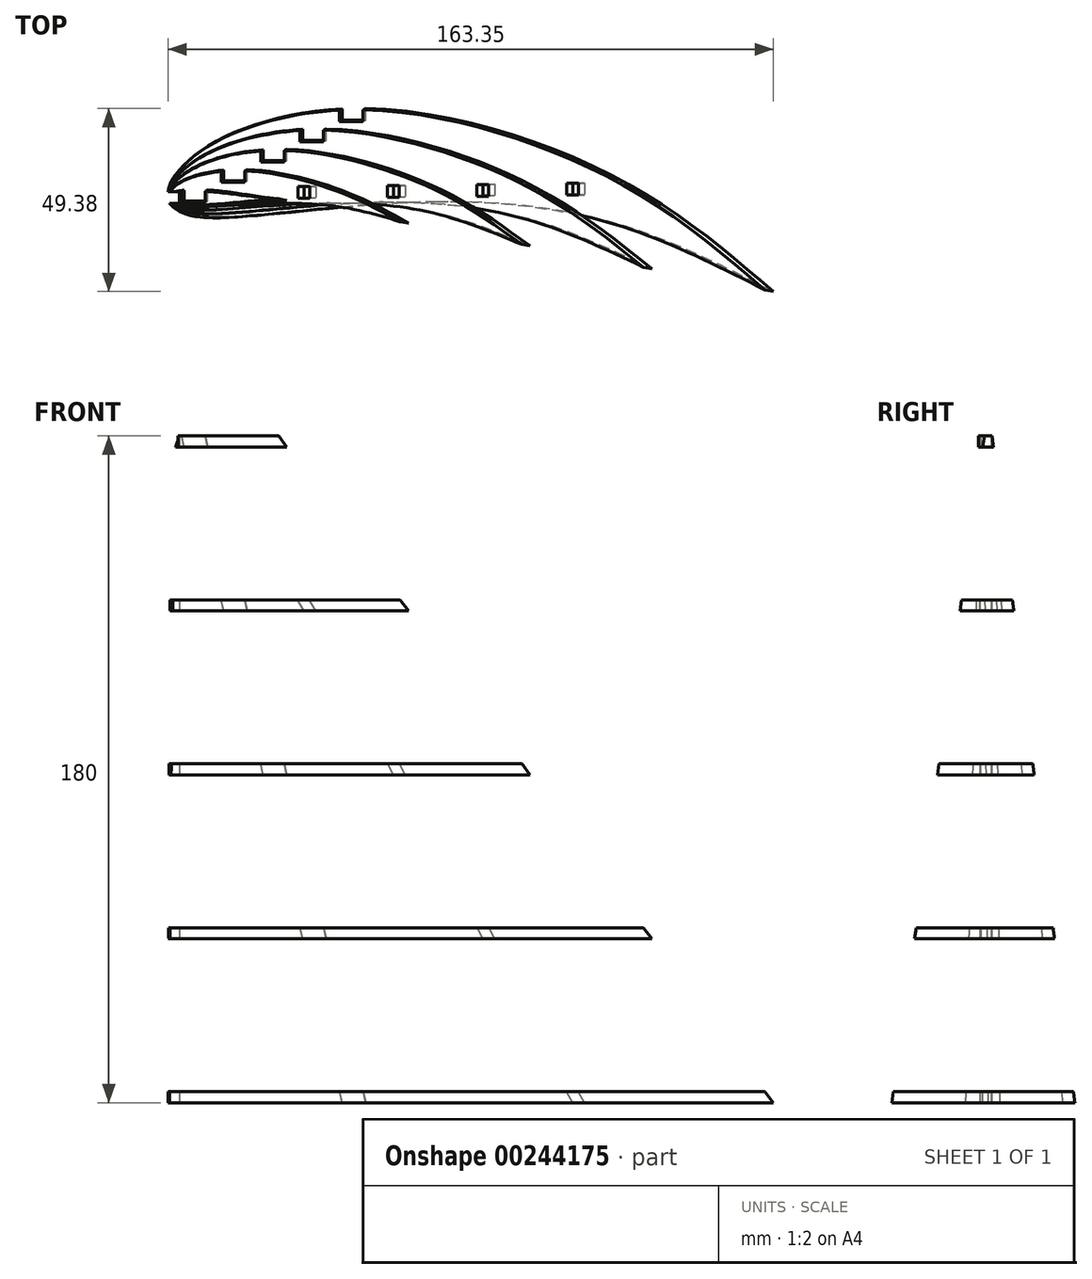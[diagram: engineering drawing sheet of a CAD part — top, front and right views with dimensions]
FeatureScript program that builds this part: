
annotation { "Feature Type Name" : "Feature", "Feature Type Description" : "" }
export const myFeature = defineFeature(function(context is Context, id is Id, definition is map)
    precondition{}
    {
        {
            var Q0;
            Q0=qCreatedBy(makeId("Top.planeOp"),FACE);
            var sketch = newSketch(context, id + "F0", { "sketchPlane" : qUnion([Q0])});
            skLineSegment(sketch, "E0", {"start": v(1.56, 5.68) * mm, "end": v(5.56, 9.57) * mm});
            skLineSegment(sketch, "E1", {"start": v(5.56, 9.57) * mm, "end": v(7.64, 11.4) * mm});
            skLineSegment(sketch, "E2", {"start": v(7.64, 11.4) * mm, "end": v(10.4, 13.54) * mm});
            skLineSegment(sketch, "E3", {"start": v(10.4, 13.54) * mm, "end": v(12.1, 14.65) * mm});
            skLineSegment(sketch, "E4", {"start": v(12.1, 14.65) * mm, "end": v(14.51, 16.01) * mm});
            skLineSegment(sketch, "E5", {"start": v(14.51, 16.01) * mm, "end": v(17.02, 17.22) * mm});
            skLineSegment(sketch, "E6", {"start": v(17.02, 17.22) * mm, "end": v(19.6, 18.28) * mm});
            skLineSegment(sketch, "E7", {"start": v(19.6, 18.28) * mm, "end": v(22.25, 19.22) * mm});
            skLineSegment(sketch, "E8", {"start": v(22.25, 19.22) * mm, "end": v(25.63, 20.25) * mm});
            skLineSegment(sketch, "E9", {"start": v(25.63, 20.25) * mm, "end": v(27.63, 20.8) * mm});
            skLineSegment(sketch, "E10", {"start": v(27.63, 20.8) * mm, "end": v(30.34, 21.45) * mm});
            skLineSegment(sketch, "E11", {"start": v(30.34, 21.45) * mm, "end": v(33.06, 22.02) * mm});
            skLineSegment(sketch, "E12", {"start": v(33.06, 22.02) * mm, "end": v(35.8, 22.52) * mm});
            skLineSegment(sketch, "E13", {"start": v(35.8, 22.52) * mm, "end": v(38.53, 22.94) * mm});
            skLineSegment(sketch, "E14", {"start": v(38.53, 22.94) * mm, "end": v(41.28, 23.3) * mm});
            skLineSegment(sketch, "E15", {"start": v(41.28, 23.3) * mm, "end": v(45.44, 23.69) * mm});
            skLineSegment(sketch, "E16", {"start": v(45.44, 23.69) * mm, "end": v(52.36, 24.01) * mm});
            skLineSegment(sketch, "E17", {"start": v(52.36, 24.01) * mm, "end": v(57.92, 23.98) * mm});
            skLineSegment(sketch, "E18", {"start": v(57.92, 23.98) * mm, "end": v(63.48, 23.67) * mm});
            skLineSegment(sketch, "E19", {"start": v(63.48, 23.67) * mm, "end": v(68.2, 23.2) * mm});
            skLineSegment(sketch, "E20", {"start": v(68.2, 23.2) * mm, "end": v(74.5, 22.25) * mm});
            skLineSegment(sketch, "E21", {"start": v(74.5, 22.25) * mm, "end": v(79.94, 21.16) * mm});
            skLineSegment(sketch, "E22", {"start": v(79.94, 21.16) * mm, "end": v(85.34, 19.84) * mm});
            skLineSegment(sketch, "E23", {"start": v(85.34, 19.84) * mm, "end": v(91.78, 17.96) * mm});
            skLineSegment(sketch, "E24", {"start": v(91.78, 17.96) * mm, "end": v(95.97, 16.57) * mm});
            skLineSegment(sketch, "E25", {"start": v(95.97, 16.57) * mm, "end": v(101.2, 14.66) * mm});
            skLineSegment(sketch, "E26", {"start": v(101.2, 14.66) * mm, "end": v(106.35, 12.57) * mm});
            skLineSegment(sketch, "E27", {"start": v(106.35, 12.57) * mm, "end": v(111.41, 10.3) * mm});
            skLineSegment(sketch, "E28", {"start": v(111.41, 10.3) * mm, "end": v(114.54, 8.79) * mm});
            skLineSegment(sketch, "E29", {"start": v(114.54, 8.79) * mm, "end": v(121.24, 5.25) * mm});
            skLineSegment(sketch, "E30", {"start": v(121.24, 5.25) * mm, "end": v(126.03, 2.48) * mm});
            skLineSegment(sketch, "E31", {"start": v(126.03, 2.48) * mm, "end": v(130.76, -0.45) * mm});
            skLineSegment(sketch, "E32", {"start": v(130.76, -0.45) * mm, "end": v(134.68, -3) * mm});
            skLineSegment(sketch, "E33", {"start": v(134.68, -3) * mm, "end": v(140.13, -6.74) * mm});
            skLineSegment(sketch, "E34", {"start": v(140.13, -6.74) * mm, "end": v(144.69, -10.02) * mm});
            skLineSegment(sketch, "E35", {"start": v(144.69, -10.02) * mm, "end": v(150.73, -14.63) * mm});
            skLineSegment(sketch, "E36", {"start": v(150.73, -14.63) * mm, "end": v(153.15, -16.57) * mm});
            skLineSegment(sketch, "E37", {"start": v(153.15, -16.57) * mm, "end": v(155.17, -18.23) * mm});
            skLineSegment(sketch, "E38", {"start": v(155.17, -18.23) * mm, "end": v(157.28, -19.98) * mm});
            skLineSegment(sketch, "E39", {"start": v(157.28, -19.98) * mm, "end": v(159.53, -21.87) * mm});
            skLineSegment(sketch, "E40", {"start": v(159.53, -21.87) * mm, "end": v(161.04, -23.14) * mm});
            skLineSegment(sketch, "E41", {"start": v(161.04, -23.14) * mm, "end": v(162.55, -24.41) * mm});
            skLineSegment(sketch, "E42", {"start": v(162.55, -24.41) * mm, "end": v(163.03, -24.83) * mm});
            skLineSegment(sketch, "E43", {"start": v(163.03, -24.83) * mm, "end": v(163.34, -25.1) * mm});
            skLineSegment(sketch, "E44", {"start": v(163.34, -25.1) * mm, "end": v(163.57, -25.34) * mm});
            skLineSegment(sketch, "E45", {"start": v(163.57, -25.34) * mm, "end": v(163.6, -25.41) * mm});
            skLineSegment(sketch, "E46", {"start": v(163.6, -25.41) * mm, "end": v(163.5, -25.38) * mm});
            skLineSegment(sketch, "E47", {"start": v(163.5, -25.38) * mm, "end": v(163.25, -25.24) * mm});
            skLineSegment(sketch, "E48", {"start": v(163.25, -25.24) * mm, "end": v(162.89, -25.02) * mm});
            skLineSegment(sketch, "E49", {"start": v(162.89, -25.02) * mm, "end": v(162.42, -24.7) * mm});
            skLineSegment(sketch, "E50", {"start": v(162.42, -24.7) * mm, "end": v(161.85, -24.33) * mm});
            skLineSegment(sketch, "E51", {"start": v(161.85, -24.33) * mm, "end": v(161.2, -23.89) * mm});
            skLineSegment(sketch, "E52", {"start": v(161.2, -23.89) * mm, "end": v(160.46, -23.39) * mm});
            skLineSegment(sketch, "E53", {"start": v(160.46, -23.39) * mm, "end": v(158.82, -22.27) * mm});
            skLineSegment(sketch, "E54", {"start": v(158.82, -22.27) * mm, "end": v(157.02, -21.04) * mm});
            skLineSegment(sketch, "E55", {"start": v(157.02, -21.04) * mm, "end": v(153.51, -18.72) * mm});
            skLineSegment(sketch, "E56", {"start": v(153.51, -18.72) * mm, "end": v(151.5, -17.45) * mm});
            skLineSegment(sketch, "E57", {"start": v(151.5, -17.45) * mm, "end": v(149.82, -16.42) * mm});
            skLineSegment(sketch, "E58", {"start": v(149.82, -16.42) * mm, "end": v(148.21, -15.5) * mm});
            skLineSegment(sketch, "E59", {"start": v(148.21, -15.5) * mm, "end": v(146.7, -14.65) * mm});
            skLineSegment(sketch, "E60", {"start": v(146.7, -14.65) * mm, "end": v(145.24, -13.9) * mm});
            skLineSegment(sketch, "E61", {"start": v(145.24, -13.9) * mm, "end": v(143.85, -13.2) * mm});
            skLineSegment(sketch, "E62", {"start": v(143.85, -13.2) * mm, "end": v(142.52, -12.6) * mm});
            skLineSegment(sketch, "E63", {"start": v(142.52, -12.6) * mm, "end": v(141.24, -12.04) * mm});
            skLineSegment(sketch, "E64", {"start": v(141.24, -12.04) * mm, "end": v(138.82, -11.11) * mm});
            skLineSegment(sketch, "E65", {"start": v(138.82, -11.11) * mm, "end": v(136.53, -10.36) * mm});
            skLineSegment(sketch, "E66", {"start": v(136.53, -10.36) * mm, "end": v(134.32, -9.76) * mm});
            skLineSegment(sketch, "E67", {"start": v(134.32, -9.76) * mm, "end": v(129.95, -8.78) * mm});
            skLineSegment(sketch, "E68", {"start": v(129.95, -8.78) * mm, "end": v(128.13, -8.4) * mm});
            skLineSegment(sketch, "E69", {"start": v(128.13, -8.4) * mm, "end": v(125.32, -7.82) * mm});
            skLineSegment(sketch, "E70", {"start": v(125.32, -7.82) * mm, "end": v(122.86, -7.3) * mm});
            skLineSegment(sketch, "E71", {"start": v(122.86, -7.3) * mm, "end": v(120.3, -6.74) * mm});
            skLineSegment(sketch, "E72", {"start": v(120.3, -6.74) * mm, "end": v(114.98, -5.62) * mm});
            skLineSegment(sketch, "E73", {"start": v(114.98, -5.62) * mm, "end": v(109.42, -4.5) * mm});
            skLineSegment(sketch, "E74", {"start": v(109.42, -4.5) * mm, "end": v(103.71, -3.46) * mm});
            skLineSegment(sketch, "E75", {"start": v(103.71, -3.46) * mm, "end": v(97.93, -2.53) * mm});
            skLineSegment(sketch, "E76", {"start": v(97.93, -2.53) * mm, "end": v(91.13, -1.7) * mm});
            skLineSegment(sketch, "E77", {"start": v(91.13, -1.7) * mm, "end": v(86.47, -1.3) * mm});
            skLineSegment(sketch, "E78", {"start": v(86.47, -1.3) * mm, "end": v(80.86, -1.04) * mm});
            skLineSegment(sketch, "E79", {"start": v(80.86, -1.04) * mm, "end": v(75.32, -0.97) * mm});
            skLineSegment(sketch, "E80", {"start": v(75.32, -0.97) * mm, "end": v(69.81, -1.08) * mm});
            skLineSegment(sketch, "E81", {"start": v(69.81, -1.08) * mm, "end": v(64.32, -1.32) * mm});
            skLineSegment(sketch, "E82", {"start": v(64.32, -1.32) * mm, "end": v(53.96, -2.02) * mm});
            skLineSegment(sketch, "E83", {"start": v(53.96, -2.02) * mm, "end": v(47.7, -2.53) * mm});
            skLineSegment(sketch, "E84", {"start": v(47.7, -2.53) * mm, "end": v(36.53, -3.57) * mm});
            skLineSegment(sketch, "E85", {"start": v(36.53, -3.57) * mm, "end": v(31.03, -4.15) * mm});
            skLineSegment(sketch, "E86", {"start": v(31.03, -4.15) * mm, "end": v(25.3, -4.8) * mm});
            skLineSegment(sketch, "E87", {"start": v(25.3, -4.8) * mm, "end": v(20.36, -5.36) * mm});
            skLineSegment(sketch, "E88", {"start": v(20.36, -5.36) * mm, "end": v(17.7, -5.56) * mm});
            skLineSegment(sketch, "E89", {"start": v(17.7, -5.56) * mm, "end": v(14.96, -5.63) * mm});
            skLineSegment(sketch, "E90", {"start": v(14.96, -5.63) * mm, "end": v(12.13, -5.52) * mm});
            skLineSegment(sketch, "E91", {"start": v(12.13, -5.52) * mm, "end": v(10.66, -5.39) * mm});
            skLineSegment(sketch, "E92", {"start": v(10.66, -5.39) * mm, "end": v(9.15, -5.2) * mm});
            skLineSegment(sketch, "E93", {"start": v(9.15, -5.2) * mm, "end": v(7.78, -4.97) * mm});
            skLineSegment(sketch, "E94", {"start": v(7.78, -4.97) * mm, "end": v(6.02, -4.6) * mm});
            skLineSegment(sketch, "E95", {"start": v(6.02, -4.6) * mm, "end": v(4.48, -4.16) * mm});
            skLineSegment(sketch, "E96", {"start": v(4.48, -4.16) * mm, "end": v(3.06, -3.62) * mm});
            skLineSegment(sketch, "E97", {"start": v(3.06, -3.62) * mm, "end": v(1.82, -2.95) * mm});
            skLineSegment(sketch, "E98", {"start": v(1.82, -2.95) * mm, "end": v(1.3, -2.56) * mm});
            skLineSegment(sketch, "E99", {"start": v(1.3, -2.56) * mm, "end": v(0.85, -2.13) * mm});
            skLineSegment(sketch, "E100", {"start": v(0.85, -2.13) * mm, "end": v(0.5, -1.66) * mm});
            skLineSegment(sketch, "E101", {"start": v(0.5, -1.66) * mm, "end": v(0.25, -1.2) * mm});
            skLineSegment(sketch, "E102", {"start": v(0.25, -1.2) * mm, "end": v(0.07, -0.6) * mm});
            skLineSegment(sketch, "E103", {"start": v(0.07, -0.6) * mm, "end": v(0, 0) * mm});
            skLineSegment(sketch, "E104", {"start": v(0, 0) * mm, "end": v(0.01, 0.63) * mm});
            skLineSegment(sketch, "E105", {"start": v(0.01, 0.63) * mm, "end": v(0.1, 1.3) * mm});
            skLineSegment(sketch, "E106", {"start": v(0.1, 1.3) * mm, "end": v(0.45, 2.7) * mm});
            skLineSegment(sketch, "E107", {"start": v(0.45, 2.7) * mm, "end": v(0.96, 4.17) * mm});
            skLineSegment(sketch, "E108", {"start": v(0.96, 4.17) * mm, "end": v(1.56, 5.68) * mm});
            skSolve(sketch);
        }
        {
            var Q0;
            Q0=qCreatedBy(makeId("Top.planeOp"),FACE);
            var sketch = newSketch(context, id + "F1", { "sketchPlane" : qUnion([Q0])});
            skPoint(sketch, "E109.0", {"position": v(0, 0) * mm});
            skPoint(sketch, "E109.1", {"position": v(0.1, 1.3) * mm});
            skPoint(sketch, "E109.2", {"position": v(0.96, 4.17) * mm});
            skPoint(sketch, "E109.3", {"position": v(10.4, 13.54) * mm});
            skPoint(sketch, "E109.4", {"position": v(52.36, 24.01) * mm});
            skPoint(sketch, "E109.5", {"position": v(121.24, 5.25) * mm});
            skPoint(sketch, "E109.6", {"position": v(163.5, -25.38) * mm});
            skPoint(sketch, "E109.7", {"position": v(0.25, -1.2) * mm});
            skPoint(sketch, "E109.8", {"position": v(3.06, -3.62) * mm});
            skPoint(sketch, "E109.9", {"position": v(12.13, -5.52) * mm});
            skPoint(sketch, "E109.10", {"position": v(64.32, -1.32) * mm});
            skPoint(sketch, "E109.11", {"position": v(120.3, -6.74) * mm});
            skFitSpline(sketch, "E110", {"points": [v(0, 0) * mm, v(0.1, 1.3) * mm, v(0.96, 4.17) * mm, v(10.4, 13.54) * mm, v(52.36, 24.01) * mm, v(121.24, 5.25) * mm, v(163.5, -25.38) * mm], "startDerivative": vector(1.58, 30.51) * mm, "endDerivative": vector(150.06, -129.12) * mm});
            skFitSpline(sketch, "E111", {"points": [v(0, 0) * mm, v(0.25, -1.2) * mm, v(3.06, -3.62) * mm, v(12.13, -5.52) * mm, v(64.32, -1.32) * mm, v(120.3, -6.74) * mm, v(163.5, -25.38) * mm], "startDerivative": vector(0.57, -28.6) * mm, "endDerivative": vector(168.26, -86.06) * mm});
            skSolve(sketch);
        }
        {
            var Q0;
            Q0=qCreatedBy(makeId("Top.planeOp"),FACE);
            cPlane(context, id + "F2", {"entities" : qUnion([Q0]), "cplaneType" : CPlaneType.OFFSET, "offset" : 180 * mm, "width" : 150 * mm, "height" : 150 * mm});
        }
        {
            var Q0;
            Q0=qCreatedBy(id+"F2.planeOp",FACE);
            var sketch = newSketch(context, id + "F3", { "sketchPlane" : qUnion([Q0])});
            skLineSegment(sketch, "E112", {"start": v(0, 0) * mm, "end": v(0.3, 0.38) * mm});
            skLineSegment(sketch, "E113", {"start": v(0.3, 0.38) * mm, "end": v(0.47, 0.56) * mm});
            skLineSegment(sketch, "E114", {"start": v(0.47, 0.56) * mm, "end": v(0.63, 0.72) * mm});
            skLineSegment(sketch, "E115", {"start": v(0.63, 0.72) * mm, "end": v(0.8, 0.86) * mm});
            skLineSegment(sketch, "E116", {"start": v(0.8, 0.86) * mm, "end": v(1, 1) * mm});
            skLineSegment(sketch, "E117", {"start": v(1, 1) * mm, "end": v(1.22, 1.1) * mm});
            skLineSegment(sketch, "E118", {"start": v(1.22, 1.1) * mm, "end": v(1.43, 1.2) * mm});
            skLineSegment(sketch, "E119", {"start": v(1.43, 1.2) * mm, "end": v(1.66, 1.26) * mm});
            skLineSegment(sketch, "E120", {"start": v(1.66, 1.26) * mm, "end": v(1.9, 1.32) * mm});
            skLineSegment(sketch, "E121", {"start": v(1.9, 1.32) * mm, "end": v(2.38, 1.4) * mm});
            skLineSegment(sketch, "E122", {"start": v(2.38, 1.4) * mm, "end": v(3.07, 1.49) * mm});
            skLineSegment(sketch, "E123", {"start": v(3.07, 1.49) * mm, "end": v(4.34, 1.61) * mm});
            skLineSegment(sketch, "E124", {"start": v(4.34, 1.61) * mm, "end": v(5.28, 1.69) * mm});
            skLineSegment(sketch, "E125", {"start": v(5.28, 1.69) * mm, "end": v(6.67, 1.76) * mm});
            skLineSegment(sketch, "E126", {"start": v(6.67, 1.76) * mm, "end": v(7.17, 1.76) * mm});
            skLineSegment(sketch, "E127", {"start": v(7.17, 1.76) * mm, "end": v(8.12, 1.75) * mm});
            skLineSegment(sketch, "E128", {"start": v(8.12, 1.75) * mm, "end": v(9.07, 1.72) * mm});
            skLineSegment(sketch, "E129", {"start": v(9.07, 1.72) * mm, "end": v(10.03, 1.66) * mm});
            skLineSegment(sketch, "E130", {"start": v(10.03, 1.66) * mm, "end": v(11.22, 1.58) * mm});
            skLineSegment(sketch, "E131", {"start": v(11.22, 1.58) * mm, "end": v(12.9, 1.43) * mm});
            skLineSegment(sketch, "E132", {"start": v(12.9, 1.43) * mm, "end": v(14.8, 1.24) * mm});
            skLineSegment(sketch, "E133", {"start": v(14.8, 1.24) * mm, "end": v(16.34, 1.07) * mm});
            skLineSegment(sketch, "E134", {"start": v(16.34, 1.07) * mm, "end": v(18.57, 0.8) * mm});
            skLineSegment(sketch, "E135", {"start": v(18.57, 0.8) * mm, "end": v(20.47, 0.56) * mm});
            skLineSegment(sketch, "E136", {"start": v(20.47, 0.56) * mm, "end": v(21.43, 0.45) * mm});
            skLineSegment(sketch, "E137", {"start": v(21.43, 0.45) * mm, "end": v(22.43, 0.33) * mm});
            skLineSegment(sketch, "E138", {"start": v(22.43, 0.33) * mm, "end": v(23.42, 0.21) * mm});
            skLineSegment(sketch, "E139", {"start": v(23.42, 0.21) * mm, "end": v(24.38, 0.1) * mm});
            skLineSegment(sketch, "E140", {"start": v(24.38, 0.1) * mm, "end": v(24.84, 0.04) * mm});
            skLineSegment(sketch, "E141", {"start": v(24.84, 0.04) * mm, "end": v(25.3, -0.01) * mm});
            skLineSegment(sketch, "E142", {"start": v(25.3, -0.01) * mm, "end": v(25.9, -0.09) * mm});
            skLineSegment(sketch, "E143", {"start": v(25.9, -0.09) * mm, "end": v(26.15, -0.12) * mm});
            skLineSegment(sketch, "E144", {"start": v(26.15, -0.12) * mm, "end": v(26.97, -0.22) * mm});
            skLineSegment(sketch, "E145", {"start": v(26.97, -0.22) * mm, "end": v(27.4, -0.27) * mm});
            skLineSegment(sketch, "E146", {"start": v(27.4, -0.27) * mm, "end": v(27.65, -0.29) * mm});
            skLineSegment(sketch, "E147", {"start": v(27.65, -0.29) * mm, "end": v(27.9, -0.3) * mm});
            skLineSegment(sketch, "E148", {"start": v(27.9, -0.3) * mm, "end": v(28.16, -0.32) * mm});
            skLineSegment(sketch, "E149", {"start": v(28.16, -0.32) * mm, "end": v(28.45, -0.34) * mm});
            skLineSegment(sketch, "E150", {"start": v(28.45, -0.34) * mm, "end": v(28.76, -0.35) * mm});
            skLineSegment(sketch, "E151", {"start": v(28.76, -0.35) * mm, "end": v(28.93, -0.36) * mm});
            skLineSegment(sketch, "E152", {"start": v(28.93, -0.36) * mm, "end": v(29.42, -0.37) * mm});
            skLineSegment(sketch, "E153", {"start": v(29.42, -0.37) * mm, "end": v(29.57, -0.37) * mm});
            skLineSegment(sketch, "E154", {"start": v(29.57, -0.37) * mm, "end": v(29.71, -0.38) * mm});
            skLineSegment(sketch, "E155", {"start": v(29.71, -0.38) * mm, "end": v(29.83, -0.38) * mm});
            skLineSegment(sketch, "E156", {"start": v(29.83, -0.38) * mm, "end": v(29.92, -0.38) * mm});
            skLineSegment(sketch, "E157", {"start": v(29.92, -0.38) * mm, "end": v(29.98, -0.38) * mm});
            skLineSegment(sketch, "E158", {"start": v(29.98, -0.38) * mm, "end": v(30, -0.39) * mm});
            skLineSegment(sketch, "E159", {"start": v(30, -0.39) * mm, "end": v(29.98, -0.39) * mm});
            skLineSegment(sketch, "E160", {"start": v(29.98, -0.39) * mm, "end": v(29.92, -0.4) * mm});
            skLineSegment(sketch, "E161", {"start": v(29.92, -0.4) * mm, "end": v(29.83, -0.4) * mm});
            skLineSegment(sketch, "E162", {"start": v(29.83, -0.4) * mm, "end": v(29.72, -0.4) * mm});
            skLineSegment(sketch, "E163", {"start": v(29.72, -0.4) * mm, "end": v(29.58, -0.4) * mm});
            skLineSegment(sketch, "E164", {"start": v(29.58, -0.4) * mm, "end": v(29.42, -0.4) * mm});
            skLineSegment(sketch, "E165", {"start": v(29.42, -0.4) * mm, "end": v(28.93, -0.42) * mm});
            skLineSegment(sketch, "E166", {"start": v(28.93, -0.42) * mm, "end": v(28.76, -0.42) * mm});
            skLineSegment(sketch, "E167", {"start": v(28.76, -0.42) * mm, "end": v(28.45, -0.43) * mm});
            skLineSegment(sketch, "E168", {"start": v(28.45, -0.43) * mm, "end": v(28.17, -0.44) * mm});
            skLineSegment(sketch, "E169", {"start": v(28.17, -0.44) * mm, "end": v(27.9, -0.46) * mm});
            skLineSegment(sketch, "E170", {"start": v(27.9, -0.46) * mm, "end": v(27.65, -0.47) * mm});
            skLineSegment(sketch, "E171", {"start": v(27.65, -0.47) * mm, "end": v(27.4, -0.49) * mm});
            skLineSegment(sketch, "E172", {"start": v(27.4, -0.49) * mm, "end": v(26.96, -0.52) * mm});
            skLineSegment(sketch, "E173", {"start": v(26.96, -0.52) * mm, "end": v(26.14, -0.6) * mm});
            skLineSegment(sketch, "E174", {"start": v(26.14, -0.6) * mm, "end": v(25.86, -0.62) * mm});
            skLineSegment(sketch, "E175", {"start": v(25.86, -0.62) * mm, "end": v(25.3, -0.68) * mm});
            skLineSegment(sketch, "E176", {"start": v(25.3, -0.68) * mm, "end": v(24.84, -0.72) * mm});
            skLineSegment(sketch, "E177", {"start": v(24.84, -0.72) * mm, "end": v(24.37, -0.77) * mm});
            skLineSegment(sketch, "E178", {"start": v(24.37, -0.77) * mm, "end": v(23.4, -0.86) * mm});
            skLineSegment(sketch, "E179", {"start": v(23.4, -0.86) * mm, "end": v(22.42, -0.95) * mm});
            skLineSegment(sketch, "E180", {"start": v(22.42, -0.95) * mm, "end": v(21.43, -1.04) * mm});
            skLineSegment(sketch, "E181", {"start": v(21.43, -1.04) * mm, "end": v(20.45, -1.13) * mm});
            skLineSegment(sketch, "E182", {"start": v(20.45, -1.13) * mm, "end": v(18.55, -1.3) * mm});
            skLineSegment(sketch, "E183", {"start": v(18.55, -1.3) * mm, "end": v(16.28, -1.52) * mm});
            skLineSegment(sketch, "E184", {"start": v(16.28, -1.52) * mm, "end": v(12.87, -1.8) * mm});
            skLineSegment(sketch, "E185", {"start": v(12.87, -1.8) * mm, "end": v(11.19, -1.9) * mm});
            skLineSegment(sketch, "E186", {"start": v(11.19, -1.9) * mm, "end": v(10, -1.95) * mm});
            skLineSegment(sketch, "E187", {"start": v(10, -1.95) * mm, "end": v(9.03, -1.98) * mm});
            skLineSegment(sketch, "E188", {"start": v(9.03, -1.98) * mm, "end": v(8.08, -1.98) * mm});
            skLineSegment(sketch, "E189", {"start": v(8.08, -1.98) * mm, "end": v(7.13, -1.96) * mm});
            skLineSegment(sketch, "E190", {"start": v(7.13, -1.96) * mm, "end": v(6.6, -1.93) * mm});
            skLineSegment(sketch, "E191", {"start": v(6.6, -1.93) * mm, "end": v(5.24, -1.83) * mm});
            skLineSegment(sketch, "E192", {"start": v(5.24, -1.83) * mm, "end": v(4.3, -1.74) * mm});
            skLineSegment(sketch, "E193", {"start": v(4.3, -1.74) * mm, "end": v(3.04, -1.58) * mm});
            skLineSegment(sketch, "E194", {"start": v(3.04, -1.58) * mm, "end": v(2.35, -1.47) * mm});
            skLineSegment(sketch, "E195", {"start": v(2.35, -1.47) * mm, "end": v(1.87, -1.37) * mm});
            skLineSegment(sketch, "E196", {"start": v(1.87, -1.37) * mm, "end": v(1.64, -1.3) * mm});
            skLineSegment(sketch, "E197", {"start": v(1.64, -1.3) * mm, "end": v(1.41, -1.22) * mm});
            skLineSegment(sketch, "E198", {"start": v(1.41, -1.22) * mm, "end": v(1.2, -1.13) * mm});
            skLineSegment(sketch, "E199", {"start": v(1.2, -1.13) * mm, "end": v(1, -1.01) * mm});
            skLineSegment(sketch, "E200", {"start": v(1, -1.01) * mm, "end": v(0.77, -0.86) * mm});
            skLineSegment(sketch, "E201", {"start": v(0.77, -0.86) * mm, "end": v(0.62, -0.73) * mm});
            skLineSegment(sketch, "E202", {"start": v(0.62, -0.73) * mm, "end": v(0.46, -0.57) * mm});
            skLineSegment(sketch, "E203", {"start": v(0.46, -0.57) * mm, "end": v(0.3, -0.38) * mm});
            skLineSegment(sketch, "E204", {"start": v(0.3, -0.38) * mm, "end": v(0, 0) * mm});
            skSolve(sketch);
        }
        {
            var Q0;
            Q0=qCreatedBy(id+"F2.planeOp",FACE);
            var sketch = newSketch(context, id + "F4", { "sketchPlane" : qUnion([Q0])});
            skPoint(sketch, "E205.0", {"position": v(0, 0) * mm});
            skPoint(sketch, "E205.1", {"position": v(0.47, 0.56) * mm});
            skPoint(sketch, "E205.2", {"position": v(0.8, 0.86) * mm});
            skPoint(sketch, "E205.3", {"position": v(1.66, 1.26) * mm});
            skPoint(sketch, "E205.4", {"position": v(8.12, 1.75) * mm});
            skPoint(sketch, "E205.5", {"position": v(21.43, 0.45) * mm});
            skPoint(sketch, "E205.6", {"position": v(30, -0.39) * mm});
            skPoint(sketch, "E205.7", {"position": v(21.43, -1.04) * mm});
            skPoint(sketch, "E205.8", {"position": v(8.08, -1.98) * mm});
            skPoint(sketch, "E205.9", {"position": v(0.46, -0.57) * mm});
            skPoint(sketch, "E205.10", {"position": v(0.77, -0.86) * mm});
            skPoint(sketch, "E205.11", {"position": v(1.64, -1.3) * mm});
            skFitSpline(sketch, "E206", {"points": [v(0, 0) * mm, v(0.47, 0.56) * mm, v(0.8, 0.86) * mm, v(1.66, 1.26) * mm, v(8.12, 1.75) * mm, v(21.43, 0.45) * mm, v(30, -0.39) * mm], "startDerivative": vector(6.64, 8.31) * mm, "endDerivative": vector(31.47, -2.67) * mm});
            skFitSpline(sketch, "E207", {"points": [v(0, 0) * mm, v(0.46, -0.57) * mm, v(0.77, -0.86) * mm, v(1.64, -1.3) * mm, v(8.08, -1.98) * mm, v(21.43, -1.04) * mm, v(30, -0.39) * mm], "startDerivative": vector(6.56, -8.44) * mm, "endDerivative": vector(31.45, 2.1) * mm});
            skSolve(sketch);
        }
        {
            var Q0;
            Q0=makeQuery(id+"F1.imprint","IMPRINT",FACE,{"disambiguationData":[TD([[makeQuery(id+"F1.imprint","IMPRINT",EDGE,{"derivedFrom":sQuery(id+"F1.wireOp",EDGE,"E110")}),-1.0]])]});
            var Q1;
            Q1=makeQuery(id+"F4.imprint","IMPRINT",FACE,{"disambiguationData":[TD([[makeQuery(id+"F4.imprint","IMPRINT",EDGE,{"derivedFrom":sQuery(id+"F4.wireOp",EDGE,"E206")}),-1.0]])]});
            loft(context, id + "F5", {"sheetProfilesArray" : [{ "sheetProfileEntities" : qUnion([Q0]) }, { "sheetProfileEntities" : qUnion([Q1]) }]});
        }
        {
            var Q0;
            Q0=makeQuery(id+"F5.opLoft","CAP_FACE",FACE,{"disambiguationData":[OSD([makeQuery(id+"F1.imprint","IMPRINT",FACE,{"disambiguationData":[TD([[makeQuery(id+"F1.imprint","IMPRINT",EDGE,{"derivedFrom":sQuery(id+"F1.wireOp",EDGE,"E110")}),-1.0]])]})])],"isStart":true});
            var sketch = newSketch(context, id + "F6", { "sketchPlane" : qUnion([Q0])});
            skLineSegment(sketch, "E208", {"start": v(0, 0) * mm, "end": v(50.35, 0) * mm, "construction": true});
            skLineSegment(sketch, "E209", {"start": v(50.35, 0) * mm, "end": v(50.35, -24) * mm, "construction": true});
            skLineSegment(sketch, "E210", {"start": v(50.35, -24) * mm, "end": v(53.52, -24) * mm, "construction": true});
            skLineSegment(sketch, "E211", {"start": v(50.35, -24) * mm, "end": v(47.17, -24) * mm, "construction": true});
            skLineSegment(sketch, "E212", {"start": v(47.17, -24) * mm, "end": v(47.17, -20.83) * mm});
            skLineSegment(sketch, "E213", {"start": v(47.17, -20.83) * mm, "end": v(53.52, -20.83) * mm});
            skLineSegment(sketch, "E214", {"start": v(53.52, -20.83) * mm, "end": v(53.52, -24) * mm});
            skLineSegment(sketch, "E215", {"start": v(53.52, -24) * mm, "end": v(53.52, -27.07) * mm});
            skLineSegment(sketch, "E216", {"start": v(53.52, -27.07) * mm, "end": v(47.17, -27.07) * mm});
            skLineSegment(sketch, "E217", {"start": v(47.17, -27.07) * mm, "end": v(47.17, -24) * mm});
            skSolve(sketch);
        }
        {
            var Q0;
            Q0=makeQuery(id+"F5.opLoft","CAP_FACE",FACE,{"disambiguationData":[OSD([makeQuery(id+"F4.imprint","IMPRINT",FACE,{"disambiguationData":[TD([[makeQuery(id+"F4.imprint","IMPRINT",EDGE,{"derivedFrom":sQuery(id+"F4.wireOp",EDGE,"E206")}),-1.0]])]})])],"isStart":true});
            var sketch = newSketch(context, id + "F7", { "sketchPlane" : qUnion([Q0])});
            skLineSegment(sketch, "E218", {"start": v(0, 0) * mm, "end": v(7, 0) * mm, "construction": true});
            skLineSegment(sketch, "E219", {"start": v(7, 0) * mm, "end": v(7, 1.78) * mm, "construction": true});
            skLineSegment(sketch, "E220", {"start": v(7, 1.78) * mm, "end": v(10.18, 1.78) * mm});
            skLineSegment(sketch, "E221", {"start": v(7, 1.78) * mm, "end": v(3.82, 1.78) * mm});
            skLineSegment(sketch, "E222", {"start": v(3.82, 1.78) * mm, "end": v(3.82, -1.4) * mm});
            skLineSegment(sketch, "E223", {"start": v(3.83, -1.4) * mm, "end": v(10.18, -1.4) * mm});
            skLineSegment(sketch, "E224", {"start": v(10.18, -1.4) * mm, "end": v(10.18, 1.78) * mm});
            skSolve(sketch);
        }
        {
            var Q0;
            Q0=sQuery(id+"F6.wireOp",VERTEX,"E213.start");
            var Q1;
            Q1=sQuery(id+"F6.wireOp",VERTEX,"E216.end");
            var Q2;
            Q2=sQuery(id+"F7.wireOp",VERTEX,"E223.start");
            cPlane(context, id + "F8", {"entities" : qUnion([Q0, Q1, Q2]), "cplaneType" : CPlaneType.THREE_POINT, "offset" : 25 * mm, "width" : 150 * mm, "height" : 150 * mm});
        }
        {
            var Q0;
            Q0=qCreatedBy(id+"F8.planeOp",FACE);
            var sketch = newSketch(context, id + "F9", { "sketchPlane" : qUnion([Q0])});
            skPoint(sketch, "E225.0", {"position": v(-20.83, -11.04) * mm});
            skPoint(sketch, "E225.1", {"position": v(1.4, 174.1) * mm});
            skLineSegment(sketch, "E226", {"start": v(-20.83, -11.04) * mm, "end": v(1.4, 174.1) * mm});
            skSolve(sketch);
        }
        {
            var Q0;
            {var subQ0=sQuery(id+"F6.wireOp",EDGE,"E215");Q0=makeQuery(id+"F6.imprint","IMPRINT",FACE,{"disambiguationData":[TD([[makeQuery(id+"F6.imprint","IMPRINT",EDGE,{"derivedFrom":subQ0}),-1.0]])]});}
            var Q1;
            {var subQ0=sQuery(id+"F6.wireOp",EDGE,"E213");Q1=makeQuery(id+"F6.imprint","IMPRINT",FACE,{"disambiguationData":[TD([[makeQuery(id+"F6.imprint","IMPRINT",EDGE,{"derivedFrom":subQ0}),-1.0]])]});}
            var Q2;
            Q2=sQuery(id+"F9.wireOp",EDGE,"E226");
            sweep(context, id + "F10", {"operationType" : NewBodyOperationType.REMOVE, "profiles" : qUnion([Q0, Q1]), "path" : qUnion([Q2])});
        }
        {
            var Q0;
            Q0=qCreatedBy(makeId("Top.planeOp"),FACE);
            var sketch = newSketch(context, id + "F11", { "sketchPlane" : qUnion([Q0])});
            skLineSegment(sketch, "E227", {"start": v(0, 0) * mm, "end": v(3.17, 0) * mm, "construction": true});
            skLineSegment(sketch, "E228", {"start": v(3.17, 0) * mm, "end": v(3.17, 1.59) * mm});
            skLineSegment(sketch, "E229", {"start": v(3.18, 1.59) * mm, "end": v(0, 1.59) * mm});
            skLineSegment(sketch, "E230", {"start": v(0, 1.59) * mm, "end": v(0, -1.59) * mm});
            skLineSegment(sketch, "E231", {"start": v(0, -1.59) * mm, "end": v(3.18, -1.59) * mm});
            skLineSegment(sketch, "E232", {"start": v(3.17, -1.59) * mm, "end": v(3.17, 0) * mm});
            skSolve(sketch);
        }
        {
            var Q0;
            Q0 = qSketchRegion(id + "F11", true);
            extrude(context, id + "F12", {"entities" : qUnion([Q0]), "operationType" : NewBodyOperationType.REMOVE, "depth" : 180 * mm, "offsetDistance" : 25 * mm});
        }
        {
            var Q0;
            Q0=qCreatedBy(makeId("Front.planeOp"),FACE);
            var sketch = newSketch(context, id + "F13", { "sketchPlane" : qUnion([Q0])});
            skLineSegment(sketch, "E233", {"start": v(0, 0) * mm, "end": v(0, 3) * mm, "construction": true});
            skLineSegment(sketch, "E234.bottom", {"start": v(0, 3) * mm, "end": v(184.5, 3) * mm});
            skLineSegment(sketch, "E234.top", {"start": v(0, 44.25) * mm, "end": v(184.5, 44.25) * mm});
            skLineSegment(sketch, "E234.left", {"start": v(0, 3) * mm, "end": v(0, 44.25) * mm});
            skLineSegment(sketch, "E234.right", {"start": v(184.5, 3) * mm, "end": v(184.5, 44.25) * mm});
            skLineSegment(sketch, "E235.0.1.0", {"start": v(0, 47.25) * mm, "end": v(184.5, 47.25) * mm});
            skLineSegment(sketch, "E235.0.1.1", {"start": v(0, 88.5) * mm, "end": v(184.5, 88.5) * mm});
            skLineSegment(sketch, "E235.0.1.2", {"start": v(0, 47.25) * mm, "end": v(0, 88.5) * mm});
            skLineSegment(sketch, "E235.0.1.3", {"start": v(184.5, 47.25) * mm, "end": v(184.5, 88.5) * mm});
            skLineSegment(sketch, "E235.0.1.4", {"start": v(0, 44.25) * mm, "end": v(0, 47.25) * mm, "construction": true});
            skLineSegment(sketch, "E235.0.2.0", {"start": v(0, 91.5) * mm, "end": v(184.5, 91.5) * mm});
            skLineSegment(sketch, "E235.0.2.1", {"start": v(0, 132.75) * mm, "end": v(184.5, 132.75) * mm});
            skLineSegment(sketch, "E235.0.2.2", {"start": v(0, 91.5) * mm, "end": v(0, 132.75) * mm});
            skLineSegment(sketch, "E235.0.2.3", {"start": v(184.5, 91.5) * mm, "end": v(184.5, 132.75) * mm});
            skLineSegment(sketch, "E235.0.2.4", {"start": v(0, 88.5) * mm, "end": v(0, 91.5) * mm, "construction": true});
            skLineSegment(sketch, "E235.0.3.0", {"start": v(0, 135.75) * mm, "end": v(184.5, 135.75) * mm});
            skLineSegment(sketch, "E235.0.3.1", {"start": v(0, 177) * mm, "end": v(184.5, 177) * mm});
            skLineSegment(sketch, "E235.0.3.2", {"start": v(0, 135.75) * mm, "end": v(0, 177) * mm});
            skLineSegment(sketch, "E235.0.3.3", {"start": v(184.5, 135.75) * mm, "end": v(184.5, 177) * mm});
            skLineSegment(sketch, "E235.0.3.4", {"start": v(0, 132.75) * mm, "end": v(0, 135.75) * mm, "construction": true});
            skLineSegment(sketch, "E235.direction1", {"start": v(0, 0) * mm, "end": v(25, 0) * mm, "construction": true});
            skLineSegment(sketch, "E235.direction2", {"start": v(0, 0) * mm, "end": v(0, 44.25) * mm, "construction": true});
            skSolve(sketch);
        }
        {
            var Q0;
            Q0 = qSketchRegion(id + "F13", true);
            extrude(context, id + "F14", {"entities" : qUnion([Q0]), "operationType" : NewBodyOperationType.REMOVE, "oppositeDirection" : true, "depth" : 100 * mm, "offsetDistance" : 25 * mm, "hasSecondDirection" : true, "secondDirectionOppositeDirection" : false, "secondDirectionDepth" : 100 * mm});
        }
        {
            var Q0;
            Q0=makeQuery(id+"F5.opLoft","CAP_FACE",FACE,{"disambiguationData":[OSD([makeQuery(id+"F1.imprint","IMPRINT",FACE,{"disambiguationData":[TD([[makeQuery(id+"F1.imprint","IMPRINT",EDGE,{"derivedFrom":sQuery(id+"F1.wireOp",EDGE,"E110")}),-1.0]])]})])],"isStart":true});
            var sketch = newSketch(context, id + "F15", { "sketchPlane" : qUnion([Q0])});
            skLineSegment(sketch, "E236.bottom", {"start": v(109.34, -3.82) * mm, "end": v(112.51, -3.82) * mm});
            skLineSegment(sketch, "E236.top", {"start": v(109.34, -0.65) * mm, "end": v(112.51, -0.65) * mm});
            skLineSegment(sketch, "E236.left", {"start": v(109.34, -3.82) * mm, "end": v(109.34, -0.65) * mm});
            skLineSegment(sketch, "E236.right", {"start": v(112.51, -3.82) * mm, "end": v(112.51, -0.65) * mm});
            skSolve(sketch);
        }
        {
            var Q0;
            Q0=makeQuery(id+"F14.boolean.opBoolean","COPY",FACE,{"derivedFrom":makeQuery(id+"F14.opExtrude","SWEPT_FACE",FACE,{"disambiguationData":[OSD([sQuery(id+"F13.wireOp",EDGE,"E235.0.3.0")])]})});
            var sketch = newSketch(context, id + "F16", { "sketchPlane" : qUnion([Q0])});
            skLineSegment(sketch, "E237.bottom", {"start": v(35.19, 3) * mm, "end": v(38.36, 3) * mm});
            skLineSegment(sketch, "E237.top", {"start": v(35.19, -0.18) * mm, "end": v(38.36, -0.18) * mm});
            skLineSegment(sketch, "E237.left", {"start": v(35.19, 3) * mm, "end": v(35.19, -0.18) * mm});
            skLineSegment(sketch, "E237.right", {"start": v(38.36, 3) * mm, "end": v(38.36, -0.18) * mm});
            skSolve(sketch);
        }
        {
            var Q0;
            Q0=sQuery(id+"F16.wireOp",VERTEX,"E237.left.end");
            var Q1;
            Q1=sQuery(id+"F15.wireOp",VERTEX,"E236.left.end");
            var Q2;
            Q2=sQuery(id+"F15.wireOp",VERTEX,"E236.bottom.start");
            cPlane(context, id + "F17", {"entities" : qUnion([Q0, Q1, Q2]), "cplaneType" : CPlaneType.THREE_POINT, "offset" : 25 * mm, "width" : 150 * mm, "height" : 150 * mm});
        }
        {
            var Q0;
            Q0=qCreatedBy(id+"F17.planeOp",FACE);
            var sketch = newSketch(context, id + "F18", { "sketchPlane" : qUnion([Q0])});
            skPoint(sketch, "E238.0", {"position": v(0.18, 102.27) * mm});
            skPoint(sketch, "E238.1", {"position": v(-0.65, -52.41) * mm});
            skLineSegment(sketch, "E239", {"start": v(0.18, 102.27) * mm, "end": v(-0.65, -52.41) * mm});
            skSolve(sketch);
        }
        {
            var Q0;
            Q0=makeQuery(id+"F15.imprint","IMPRINT",FACE,{"disambiguationData":[TD([[makeQuery(id+"F15.imprint","IMPRINT",EDGE,{"derivedFrom":sQuery(id+"F15.wireOp",EDGE,"E236.bottom")}),1.0]])]});
            var Q1;
            Q1=sQuery(id+"F18.wireOp",EDGE,"E239");
            sweep(context, id + "F19", {"operationType" : NewBodyOperationType.REMOVE, "profiles" : qUnion([Q0]), "path" : qUnion([Q1])});
        }
    });
